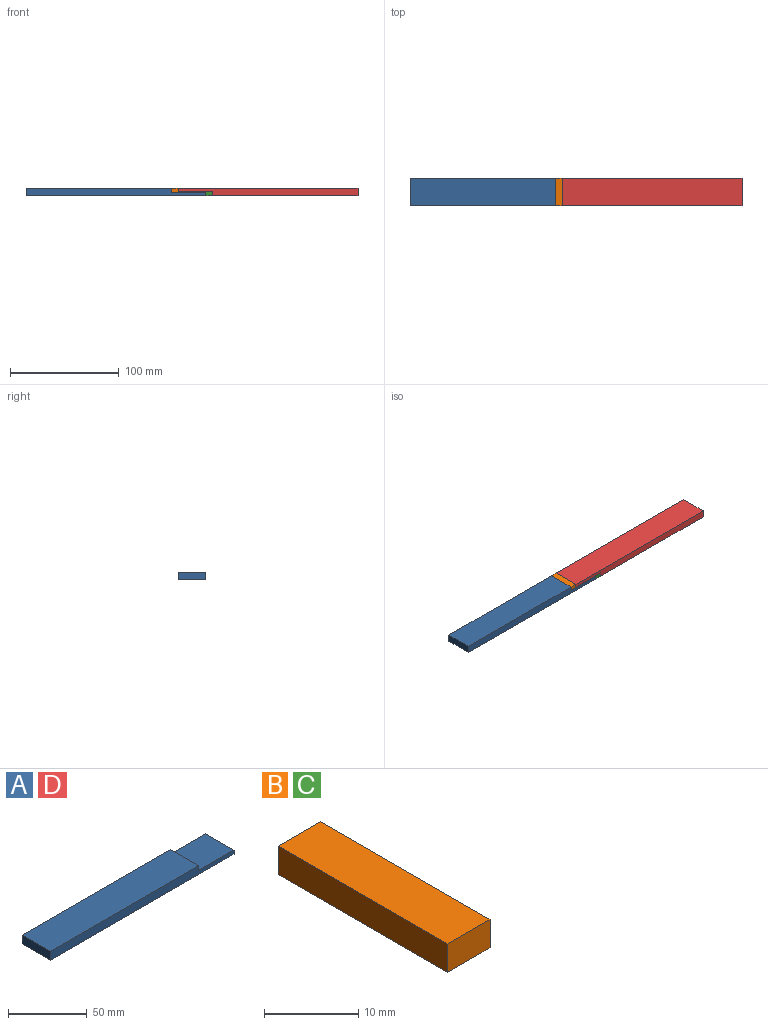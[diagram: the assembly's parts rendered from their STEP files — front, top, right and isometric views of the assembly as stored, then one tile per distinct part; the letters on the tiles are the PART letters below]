
ASSEMBLY  parts=4 mates=9
PART A: 8 faces, bbox 165.1x25.4x6.9 mm
  f0: plane 25.4x6.86mm, normal (-1,0,0), area 174.2mm2, adj f1,f5,f6,f7
  f1: plane 165.1x25.4mm, normal (0,0,-1), area 4193.5mm2, adj f0,f2,f6,f7
  f2: plane 25.4x3.18mm, normal (1,0,0), area 80.6mm2, adj f1,f3,f6,f7
  f3: plane 31.75x25.4mm, normal (0,0,1), area 806.5mm2, adj f2,f4,f6,f7
  f4: plane 25.4x3.68mm, normal (1,0,0), area 93.5mm2, adj f3,f5,f6,f7
  f5: plane 133.35x25.4mm, normal (0,0,1), area 3387.1mm2, adj f0,f4,f6,f7
  f6: plane 165.1x6.86mm, normal (0,-1,0), area 1015.3mm2, adj f0,f1,f2,f3,f4,f5
  f7: plane 165.1x6.86mm, normal (0,1,0), area 1015.3mm2, adj f0,f1,f2,f3,f4,f5
PART B: 6 faces, bbox 6.4x25.4x3.7 mm
  f0: plane 25.4x6.35mm, normal (0,0,1), area 161.3mm2, adj f1,f3,f4,f5
  f1: plane 25.4x3.68mm, normal (-1,0,0), area 93.5mm2, adj f0,f2,f4,f5
  f2: plane 25.4x6.35mm, normal (0,0,-1), area 161.3mm2, adj f1,f3,f4,f5
  f3: plane 25.4x3.68mm, normal (1,0,0), area 93.5mm2, adj f0,f2,f4,f5
  f4: plane 6.35x3.68mm, normal (0,-1,0), area 23.4mm2, adj f0,f1,f2,f3
  f5: plane 6.35x3.68mm, normal (0,1,0), area 23.4mm2, adj f0,f1,f2,f3
PART C: same geometry as B
PART D: same geometry as A
PLACE A rot(axis=(0,1,0),0deg) t=(-43.5,44.96,-46.13)mm
PLACE B rot(axis=(0,1,0),0deg) t=(26.35,44.96,-41.11)mm
PLACE C rot(axis=(0,1,0),0deg) t=(58.1,44.96,-44.29)mm
PLACE D rot(axis=(0,-1,0),180deg) t=(127.95,44.96,-39.27)mm
MATE planar D.f2 <-> B.f3  axis (-1,0,0) through (29.53,32.26,-40.86)mm
MATE planar A.f6 <-> D.f6  axis (0,-1,0) through (-27.62,19.56,-46.13)mm
MATE planar A.f5 <-> D.f1  axis (0,0,1) through (-43.5,32.26,-39.27)mm
MATE planar B.f0 <-> A.f5  axis (0,0,1) through (29.53,32.26,-39.27)mm
MATE planar C.f4 <-> D.f6  axis (0,-1,0) through (58.1,19.56,-44.29)mm
MATE planar C.f0 <-> D.f3  axis (0,0,1) through (61.28,32.26,-42.45)mm
MATE planar B.f4 <-> A.f6  axis (0,-1,0) through (26.35,19.56,-41.11)mm
MATE planar A.f4 <-> B.f1  axis (1,0,0) through (23.18,32.26,-41.11)mm
MATE planar A.f2 <-> C.f1  axis (1,0,0) through (54.93,32.26,-44.54)mm
